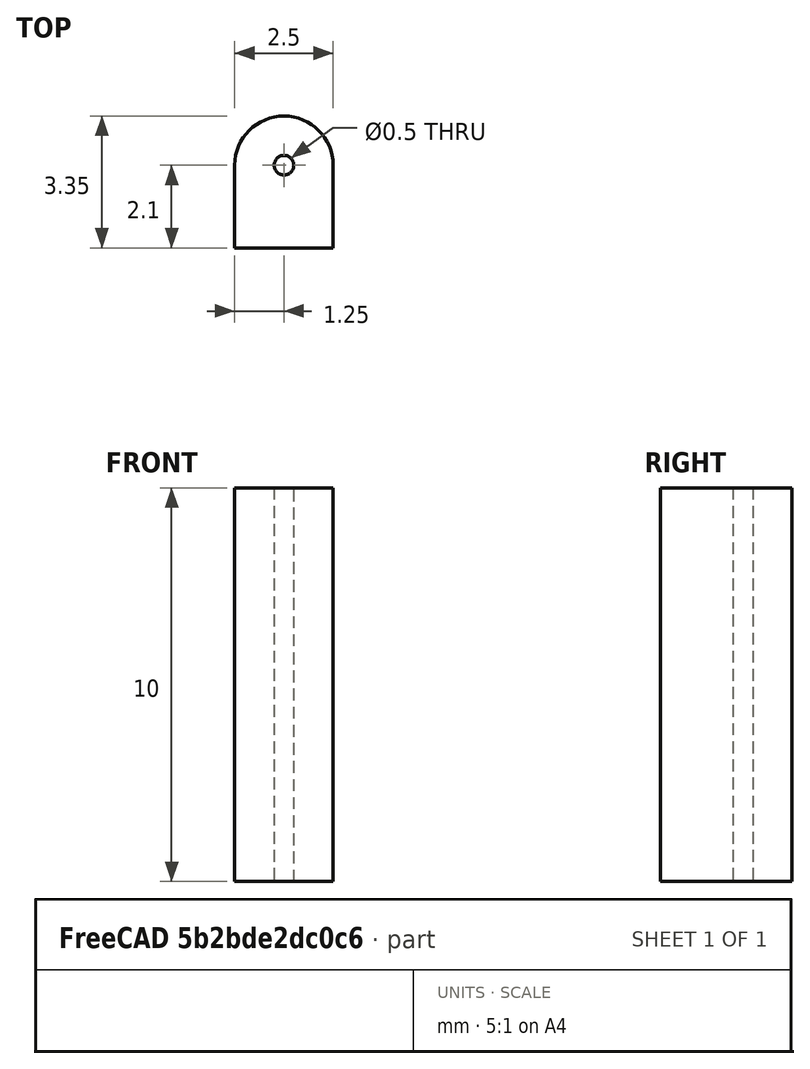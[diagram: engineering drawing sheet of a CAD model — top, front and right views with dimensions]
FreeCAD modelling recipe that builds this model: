
FCSTD DOCUMENT  (FreeCAD 0.21R33668 +26 (Git))
Label: hinge
License: All rights reserved
LicenseURL: http://en.wikipedia.org/wiki/All_rights_reserved
objects: Sketcher::SketchObject×1, PartDesign::Pad×1, PartDesign::Body×1
note: 4 computed .brp shape members not serialized (recipe doc carries the construction recipe); baked Part::Feature solids carry a one-line shape summary decoded from their .brp

FEATURE [Sketcher::SketchObject] Sketch
  FullyConstrained = true
  MapMode = 5
  Support = -> [XY_Plane]
  sketch-geometry (5):
    g0: LineSegment StartX=9e-16 StartY=2e-16 StartZ=0 EndX=0 EndY=-2.1 EndZ=0
    g1: LineSegment StartX=0 StartY=-2.1 StartZ=0 EndX=2.5 EndY=-2.1 EndZ=0
    g2: LineSegment StartX=2.5 StartY=-2.1 StartZ=0 EndX=2.5 EndY=-1.2879e-12 EndZ=0
    g3: ArcOfCircle CenterX=1.25 CenterY=0 CenterZ=0 NormalX=0 NormalY=0 NormalZ=1 AngleXU=0 Radius=1.25 StartAngle=-1.0303e-12 EndAngle=3.14159
    g4: Circle CenterX=1.25 CenterY=0 CenterZ=0 NormalX=0 NormalY=0 NormalZ=1 AngleXU=0 Radius=0.25
  constraints (14):
    c: Coincident(g0,g-1)
    c: PointOnObject(g0,g-2)
    c: Coincident(g1,g0)
    c: Horizontal(g1)
    c: Coincident(g2,g1)
    c: PointOnObject(g2,g-1)
    c: Vertical(g2)
    c: DistanceX(g1,g1) = 2.5
    c: DistanceY(g2,g2) = 2.1
    c: Coincident(g3,g0)
    c: Coincident(g3,g2)
    c: DistanceY(g0,g3) = 0
    c: Coincident(g4,g3)
    c: Diameter(g4) = 0.5
FEATURE [PartDesign::Pad] Pad
  Direction = (0,0,1)
  Length = 10
  Length2 = 10
  Profile = -> Sketch
  ReferenceAxis = -> Sketch [N_Axis]
  Type = 0
FEATURE [PartDesign::Body] Body
  Group = -> [Sketch,Pad]
  Origin = -> Origin
  Tip = -> Pad
